# Revit family: Стайл_Eng
name_source: partatom
category: Mechanical Equipment
units: mm (PartAtom-declared; Revit-internal decimal feet)

## family parameters
Always vertical = Yes
Classification = None
Cut with Voids When Loaded = No
Part Type = Normal
Room Calculation Point = No
Round Connector Dimension = Use Diameter
Shared = No
Work Plane-Based = No

## types (1)
- 100 Style
    00_20_Manufacturer = Vents
    00_20_Name = Axial fan
    00_20_Type = 100 Style
    Amperage = 0 A
    B = 175 mm  [stored 0.574147 ft]
    Casing Material = Plastic, opaque, white
    D = 100 mm  [stored 0.328084 ft]
    Default Elevation = 0 mm  [stored 0 ft]
    Diameter = 100 mm  [stored 0.328084 ft]
    Dy = 95 mm
    Frequency = 50 Hz
    H = 221 mm  [stored 0.725066 ft]
    Height = 221 mm  [stored 0.725066 ft]
    L = 77 mm  [stored 0.252625 ft]
    L1 = 39 mm  [stored 0.127953 ft]
    L2 = 38 mm  [stored 0.124672 ft]
    Length = 77 mm  [stored 0.252625 ft]
    Load Classification = HVAC
    Maintenance zone material = <By Category>
    Manufacturer = Vents
    Maximum Air Flow = 97.0 m³/h
    Number of Fase = 1
    Power = 9 W
    Sound pressure level at 3 m distance = 25 dBA
    URL = https://ventilation-system.com
    Voltage = 230 V
    Weight = 0.55 kg
    Width = 175 mm  [stored 0.574147 ft]

note: [stored X ft] marks values corroborated as IEEE doubles in the binary element streams (Revit-internal decimal feet)
